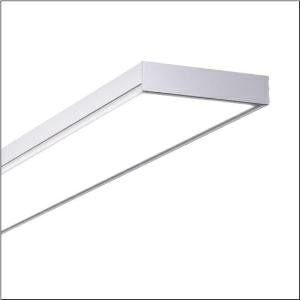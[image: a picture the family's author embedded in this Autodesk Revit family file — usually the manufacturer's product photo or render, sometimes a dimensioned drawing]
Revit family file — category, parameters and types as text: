
# Revit family: apollon_31_surface_51mp25wd2441e
name_source: partatom
category: Lighting Fixtures
units: mm (PartAtom-declared; Revit-internal decimal feet)

## family parameters
Cut with Voids When Loaded = No
Host = Face
Light Source = No
Part Type = Normal
Room Calculation Point = No
Round Connector Dimension = Use Diameter
Shared = No

## types (1)
- Apollon 31 Surface (1 x LED, 3800 lm, 28 W, 4000K)
    Apparent Load = 28 VA
    CIE Flux Codes = 61 87 97 97 100
    Color Rendering = 80
    Color Temperature = 4000K
    Default Elevation = 1800 mm
    Description = Apollon 31 Surface, office luminaire, primary optical cover: micro prismatic cover, of PMMA, light emission: direct distribution, primary light characteristic: symmetric, installation type: surface-mounted, LED, rated luminous flux: 3.800lm, luminous efficacy: 134lm/W, light colour: 840, colour temperature: 4000K, control gear: DALI 2, with terminal, 5-pole, mains connection: 220..240V, AC, 50/60Hz, rated input power: 28W, housing, of sheet steel, coated, metallic grey (RAL 9006), length: 1.245mm, width: 200mm, height: 44mm, protection rating (complete): IP20, protection rating (on room side): IP40, protection rating (lamp compartment, on room side): IP40, insulation class (complete): insulation class I (protective earthing), certification: CE, ENEC, UKCA, impact resistance: IK02, permissible operating ambient temperature: -20..+40°C, standard: EN 60598-2-22, packaging unit: 1 piece
    Height = 44 mm
    Lamp = 1 x LED
    Lamp Light Flux = 3800 lm
    Lamp Power = 28 W
    Lamp count = 1
    Length = 1245 mm
    Luminous efficacy = 136 lm/W
    Manufacturer = Siteco
    ModVariant = No
    Model = 51MP25WD2441E
    Mounting Place = Ceiling
    Mounting Type = Surface mounted
    Number of Poles = 1
    OnlyDefault = Yes
    Power Factor = 1
    Product Name = Apollon 31 Surface
    Product group = office luminaire | ceiling mounted
    ProductGroupID = 301
    Protection Class = Protection class I
    Protection Degree = IP 20
    RLX_Detail_Level = 1
    RLX_Emergency_Light_Flux = 0 lm
    RLX_Emergency_Type = 0
    RLX_Emergency_Type_DB = No
    RlxData = <blob elided: 24153 chars, md5=aad6567f>
    Socket = socket
    Standby Power = 0 W
    System Light Flux = 3800 lm
    System Power = 28 W
    Type Comments = Product without accessories
    Type Image = l_1313654.jpg
    URL = http://relux.com
    VarID = ---
    Voltage = 0 V
    Weight = 0.00 kg
    Width = 200 mm  [stored 0.656168 ft]

note: [stored X ft] marks values corroborated as IEEE doubles in the binary element streams (Revit-internal decimal feet)

## geometry (parser evidence)
native form markers: Blend x4, Sweep x9
no freeform markers — native parametric forms only
